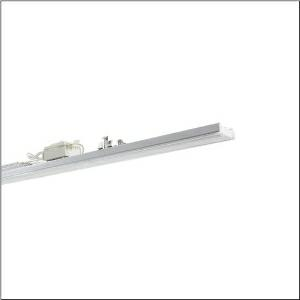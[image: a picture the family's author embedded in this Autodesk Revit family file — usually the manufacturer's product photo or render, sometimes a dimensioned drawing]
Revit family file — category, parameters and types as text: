
# Revit family: licross_r__11_recessed_ho_51te12dn4exm_b7b2
name_source: partatom
category: Lighting Fixtures
units: mm (PartAtom-declared; Revit-internal decimal feet)

## family parameters
Cut with Voids When Loaded = No
Host = Face
Light Source = No
Part Type = Normal
Room Calculation Point = No
Round Connector Dimension = Use Diameter
Shared = No

## types (1)
- --- (1 x LED, 14030 lm, 76.8 W, 4000K)
    Apparent Load = 77 VA
    CIE Flux Codes = 66 91 98 100 100
    Color Rendering = 80
    Color Temperature = 4000K
    Default Elevation = 1800 mm
    Description = Licross® 11 Recessed HO, luminaire insert, of sheet steel, galvanised, coil coated, white, length: 1.500mm, width: 66mm, height: 67mm, LED rated luminous flux: 14.030lm, light colour: 840, control gear: DALI 2, with plug, 5-pole, with phase selection, mains connection: 220..240V, AC, 50/60Hz, rated input power: 77W, halogen-free wiring, primary optical cover: cover, of PMMA, light emission: direct distribution, primary light characteristic: symmetric, protection rating (complete): IP54, insulation class (complete): insulation class I (protective earthing), certification: CE, ENEC, VDE, UKCA, protection symbol: D if used in an environment with non-conductive dust loads with corresponding accessories, impact resistance: IK06, permissible ambient temperature for indoor applications: -25..+30°C, corresponds to IFS (International Featured Standards) requirements for safety and quality in the food industry, reducing of maximum allowable ambient temperature of 5°C with ceiling mounting, LABS conformity tested according to VDMA 24364:2018-05, packaging unit: 1 piece
    Height = 58 mm
    Lamp = 1 x LED
    Lamp Light Flux = 14030 lm
    Lamp Power = 76.8 W
    Lamp count = 1
    Length = 1500 mm
    Luminous efficacy = 183 lm/W
    Manufacturer = Siteco
    ModVariant = No
    Model = 51TE12DN4EXM
    Mounting Place = Ceiling
    Mounting Type = Pendant
    Number of Poles = 1
    OnlyDefault = Yes
    Power Factor = 1
    Product Name = Licross® 11 Recessed HO
    Product group = luminaire insert
    ProductGroupID = 902
    Protection Class = Protection class I
    Protection Degree = IP 54
    RLX_Detail_Level = 1
    RLX_Emergency_Light_Flux = 0 lm
    RLX_Emergency_Type = 0
    RLX_Emergency_Type_DB = No
    RlxData = <blob elided: 24573 chars, md5=e630af34>
    Socket = socket
    Standby Power = 0 W
    System Light Flux = 14030 lm
    System Power = 77 W
    Type Comments = factory setting: luminous flux: 100 % | dim-lin: 254 | 522 mA
    Type Image = l_1296930.jpg
    URL = http://relux.com
    VarID = @adj_099570
    Voltage = 0 V
    Weight = 0.00 kg
    Width = 66 mm

## geometry (parser evidence)
native form markers: Blend x4, Sweep x12
no freeform markers — native parametric forms only
